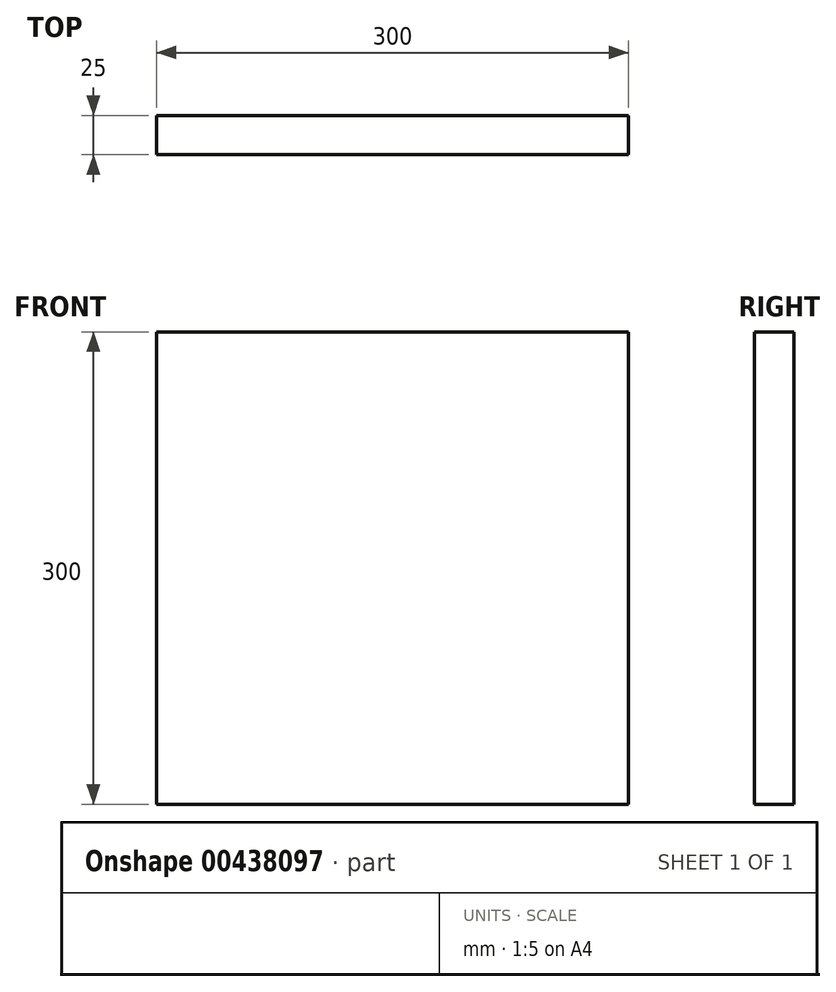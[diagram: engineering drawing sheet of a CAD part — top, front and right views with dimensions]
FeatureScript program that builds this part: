
annotation { "Feature Type Name" : "Feature", "Feature Type Description" : "" }
export const myFeature = defineFeature(function(context is Context, id is Id, definition is map)
    precondition{}
    {
        {
            var Q0;
            Q0=qCreatedBy(makeId("Front.planeOp"),FACE);
            var sketch = newSketch(context, id + "F0", { "sketchPlane" : qUnion([Q0])});
            skLineSegment(sketch, "E0.bottom", {"start": v(-162.66, -149.7) * mm, "end": v(137.34, -149.7) * mm});
            skLineSegment(sketch, "E0.top", {"start": v(-162.66, 150.3) * mm, "end": v(137.34, 150.3) * mm});
            skLineSegment(sketch, "E0.left", {"start": v(-162.66, -149.7) * mm, "end": v(-162.66, 150.3) * mm});
            skLineSegment(sketch, "E0.right", {"start": v(137.34, -149.7) * mm, "end": v(137.34, 150.3) * mm});
            skSolve(sketch);
        }
        {
            var Q0;
            Q0=makeQuery(id+"F0.imprint","IMPRINT",FACE,{"disambiguationData":[TD([[makeQuery(id+"F0.imprint","IMPRINT",EDGE,{"derivedFrom":sQuery(id+"F0.wireOp",EDGE,"E0.bottom")}),1.0]])]});
            extrude(context, id + "F1", {"entities" : qUnion([Q0]), "depth" : 25 * mm, "offsetDistance" : 25 * mm});
        }
    });
